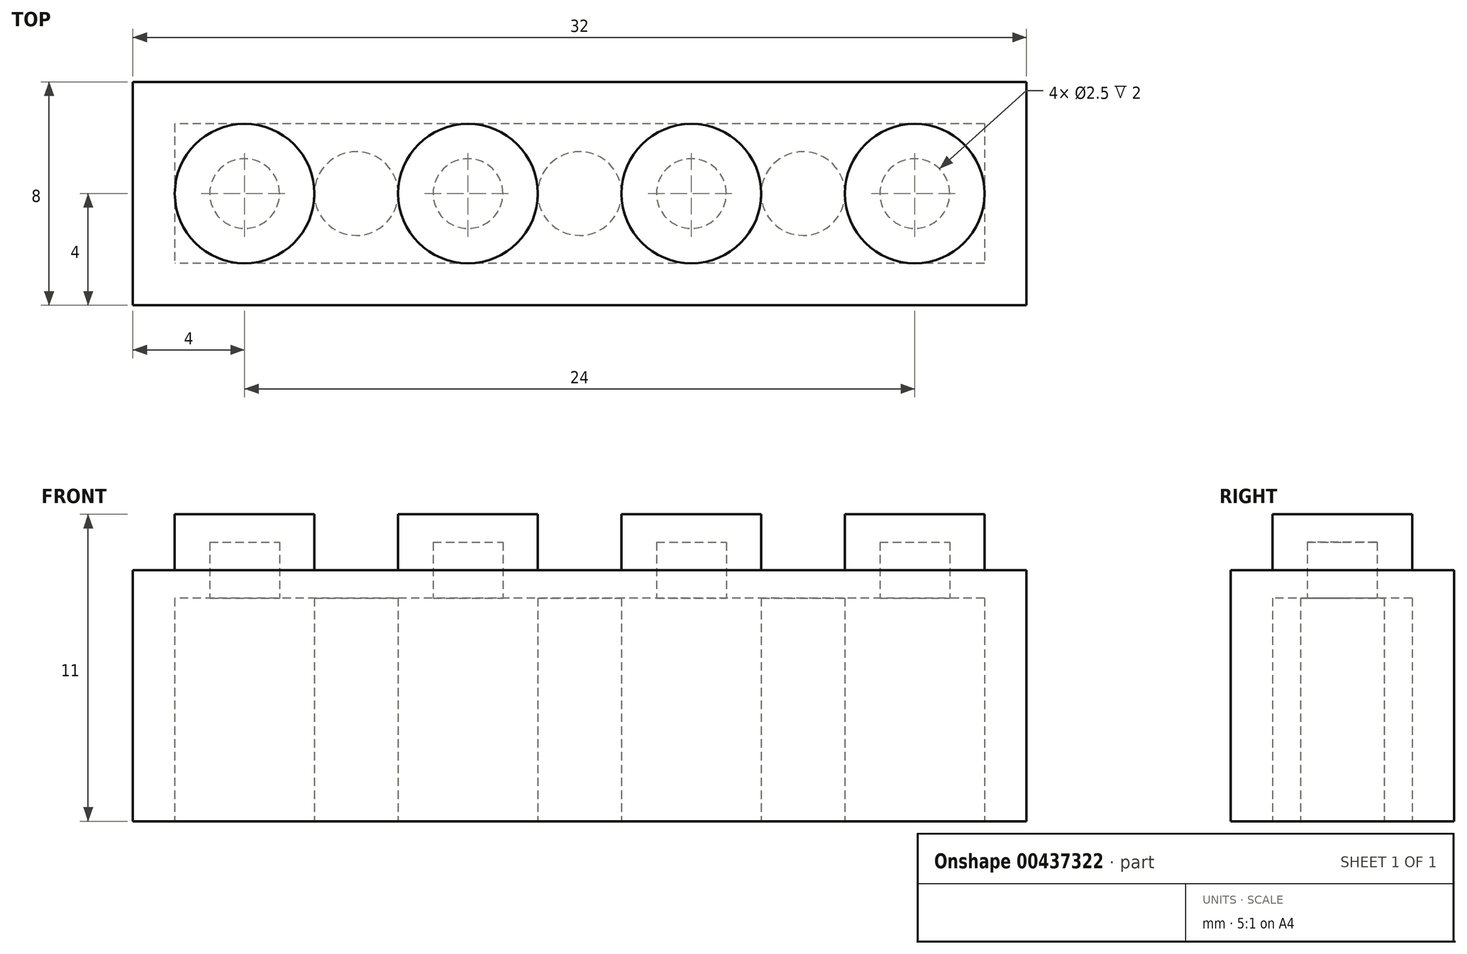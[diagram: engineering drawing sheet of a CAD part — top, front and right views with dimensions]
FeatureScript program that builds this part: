
annotation { "Feature Type Name" : "Feature", "Feature Type Description" : "" }
export const myFeature = defineFeature(function(context is Context, id is Id, definition is map)
    precondition{}
    {
        {
            var Q0;
            Q0=qCreatedBy(makeId("Front.planeOp"),FACE);
            var sketch = newSketch(context, id + "F0", { "sketchPlane" : qUnion([Q0])});
            skLineSegment(sketch, "E0.bottom", {"start": v(16, -4.5) * mm, "end": v(-16, -4.5) * mm});
            skLineSegment(sketch, "E0.top", {"start": v(16, 4.5) * mm, "end": v(-16, 4.5) * mm});
            skLineSegment(sketch, "E0.left", {"start": v(16, -4.5) * mm, "end": v(16, 4.5) * mm});
            skLineSegment(sketch, "E0.right", {"start": v(-16, -4.5) * mm, "end": v(-16, 4.5) * mm});
            skPoint(sketch, "E0.middle", {"position": v(0, 0) * mm});
            skSolve(sketch);
        }
        {
            var Q0;
            Q0=qSketchRegion(id+"F0",true);
            extrude(context, id + "F1", {"entities" : qUnion([Q0]), "oppositeDirection" : true, "depth" : 8 * mm});
        }
        {
            var Q0;
            Q0=makeQuery(id+"F1.opExtrude","SWEPT_FACE",FACE,{"disambiguationData":[OSD([sQuery(id+"F0.wireOp",EDGE,"E0.top")])]});
            var sketch = newSketch(context, id + "F2", { "sketchPlane" : qUnion([Q0])});
            skCircle(sketch, "E1", {"center": v(-12, 4) * mm, "radius": 2.5 * mm});
            skCircle(sketch, "E2.1.0.0", {"center": v(-4, 4) * mm, "radius": 2.5 * mm});
            skCircle(sketch, "E2.2.0.0", {"center": v(4, 4) * mm, "radius": 2.5 * mm});
            skCircle(sketch, "E2.3.0.0", {"center": v(12, 4) * mm, "radius": 2.5 * mm});
            skLineSegment(sketch, "E2.direction1", {"start": v(-12, 4) * mm, "end": v(-4, 4) * mm, "construction": true});
            skSolve(sketch);
        }
        {
            var Q0;
            Q0=makeQuery(id+"F2.imprint","IMPRINT",FACE,{"disambiguationData":[TD([[makeQuery(id+"F2.imprint","IMPRINT",EDGE,{"derivedFrom":sQuery(id+"F2.wireOp",EDGE,"E1")}),1.0]])]});
            var Q1;
            Q1=makeQuery(id+"F2.imprint","IMPRINT",FACE,{"disambiguationData":[TD([[makeQuery(id+"F2.imprint","IMPRINT",EDGE,{"derivedFrom":sQuery(id+"F2.wireOp",EDGE,"E2.1.0.0")}),1.0]])]});
            var Q2;
            Q2=makeQuery(id+"F2.imprint","IMPRINT",FACE,{"disambiguationData":[TD([[makeQuery(id+"F2.imprint","IMPRINT",EDGE,{"derivedFrom":sQuery(id+"F2.wireOp",EDGE,"E2.2.0.0")}),1.0]])]});
            var Q3;
            Q3=makeQuery(id+"F2.imprint","IMPRINT",FACE,{"disambiguationData":[TD([[makeQuery(id+"F2.imprint","IMPRINT",EDGE,{"derivedFrom":sQuery(id+"F2.wireOp",EDGE,"E2.3.0.0")}),1.0]])]});
            extrude(context, id + "F3", {"entities" : qUnion([Q0, Q1, Q2, Q3]), "operationType" : NewBodyOperationType.ADD, "depth" : 2 * mm});
        }
        {
            var Q0;
            Q0=makeQuery(id+"F1.opExtrude","SWEPT_FACE",FACE,{"disambiguationData":[OSD([sQuery(id+"F0.wireOp",EDGE,"E0.bottom")])]});
            var sketch = newSketch(context, id + "F4", { "sketchPlane" : qUnion([Q0])});
            skLineSegment(sketch, "E3.bottom", {"start": v(14.5, -6.5) * mm, "end": v(-14.5, -6.5) * mm});
            skLineSegment(sketch, "E3.top", {"start": v(14.5, -1.5) * mm, "end": v(-14.5, -1.5) * mm});
            skLineSegment(sketch, "E3.left", {"start": v(14.5, -6.5) * mm, "end": v(14.5, -1.5) * mm});
            skLineSegment(sketch, "E3.right", {"start": v(-14.5, -6.5) * mm, "end": v(-14.5, -1.5) * mm});
            skPoint(sketch, "E3.middle", {"position": v(0, -4) * mm});
            skPoint(sketch, "E3.middle.positionSnap0", {"position": v(0, 0) * mm});
            skPoint(sketch, "E3.centerSnap0", {"position": v(0, 0) * mm});
            skCircle(sketch, "E4", {"center": v(0, -4) * mm, "radius": 1.5 * mm});
            skCircle(sketch, "E5", {"center": v(8, -4) * mm, "radius": 1.5 * mm});
            skCircle(sketch, "E6", {"center": v(-8, -4) * mm, "radius": 1.5 * mm});
            skSolve(sketch);
        }
        {
            var Q0;
            Q0=makeQuery(id+"F4.imprint","IMPRINT",FACE,{"disambiguationData":[TD([[makeQuery(id+"F4.imprint","IMPRINT",EDGE,{"derivedFrom":sQuery(id+"F4.wireOp",EDGE,"E3.bottom")}),-1.0]])]});
            extrude(context, id + "F5", {"entities" : qUnion([Q0]), "operationType" : NewBodyOperationType.REMOVE, "oppositeDirection" : true, "depth" : 8 * mm});
        }
        {
            var Q0;
            {var subQ1=sQuery(id+"F0.wireOp",EDGE,"E0.left");var subQ3=sQuery(id+"F0.wireOp",EDGE,"E0.bottom");Q0=makeQuery(id+"F5.boolean.opBoolean","SPLIT",FACE,{"disambiguationData":[TD([makeQuery(id+"F1.opExtrude","SWEPT_FACE",FACE,{"disambiguationData":[OSD([subQ1])]})])],"derivedFrom":makeQuery(id+"F1.opExtrude","SWEPT_FACE",FACE,{"disambiguationData":[OSD([subQ3])]})});}
            var sketch = newSketch(context, id + "F6", { "sketchPlane" : qUnion([Q0])});
            skCircle(sketch, "E7", {"center": v(-12, -4) * mm, "radius": 1.25 * mm});
            skCircle(sketch, "E8", {"center": v(-4, -4) * mm, "radius": 1.25 * mm});
            skCircle(sketch, "E9", {"center": v(4, -4) * mm, "radius": 1.25 * mm});
            skCircle(sketch, "E10", {"center": v(12, -4) * mm, "radius": 1.25 * mm});
            skSolve(sketch);
        }
        {
            var Q0;
            Q0=makeQuery(id+"F6.imprint","IMPRINT",FACE,{"disambiguationData":[TD([[makeQuery(id+"F6.imprint","IMPRINT",EDGE,{"derivedFrom":sQuery(id+"F6.wireOp",EDGE,"E7")}),1.0]])]});
            var Q1;
            Q1=makeQuery(id+"F6.imprint","IMPRINT",FACE,{"disambiguationData":[TD([[makeQuery(id+"F6.imprint","IMPRINT",EDGE,{"derivedFrom":sQuery(id+"F6.wireOp",EDGE,"E8")}),1.0]])]});
            var Q2;
            Q2=makeQuery(id+"F6.imprint","IMPRINT",FACE,{"disambiguationData":[TD([[makeQuery(id+"F6.imprint","IMPRINT",EDGE,{"derivedFrom":sQuery(id+"F6.wireOp",EDGE,"E9")}),1.0]])]});
            var Q3;
            Q3=makeQuery(id+"F6.imprint","IMPRINT",FACE,{"disambiguationData":[TD([[makeQuery(id+"F6.imprint","IMPRINT",EDGE,{"derivedFrom":sQuery(id+"F6.wireOp",EDGE,"E10")}),1.0]])]});
            extrude(context, id + "F7", {"entities" : qUnion([Q0, Q1, Q2, Q3]), "operationType" : NewBodyOperationType.REMOVE, "oppositeDirection" : true, "depth" : 10 * mm});
        }
    });
